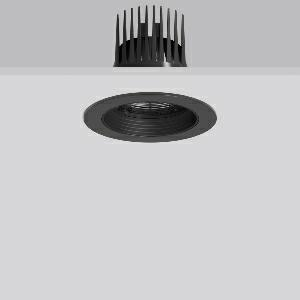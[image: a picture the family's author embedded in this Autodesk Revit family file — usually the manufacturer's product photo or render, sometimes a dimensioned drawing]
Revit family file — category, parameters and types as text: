
# Revit family: heledon_maxi_e_901781_003_3351
name_source: partatom
category: Lighting Fixtures
units: mm (PartAtom-declared; Revit-internal decimal feet)

## family parameters
Cut with Voids When Loaded = No
Host = Face
Light Source = No
Part Type = Normal
Room Calculation Point = No
Round Connector Dimension = Use Diameter
Shared = No

## types (1)
- HELEDON maxi E (1 x LED Modul 920 meat+, 1900 lm, 2000)
    Apparent Load = 33 VA
    Approval mark = CE
    CIE Flux Codes = 97 100 100 100 100
    Color Rendering = 90
    Color Temperature = 2000
    Default Elevation = 1800 mm
    Description = Series: HELEDON maxi
Round recessed downlight. Housing: die-cast aluminium, powder-coated. Black plastic ring and recessed LED to prevent glare from the side. Optical assembly with lens made of plastic (polycarbonate) for the best homogeneous light distribution - can be changed without tools. Special LED for illumination of meat included. Suitable for Recessed ceiling mounting. Installation without tools thanks to spring fastening system. Including separate LED converter with connecting cable 600 mm.High quality converter without flickering and stroboscopic effect. Through-wiring box (5 pole) available as accessory. The following accessories can be mounted without use of tools: interchangeable lenses, decorative glasses, honeycomb louvre, clear and frosted diffusers, white interchangeable plastic ring. 
Colour: deep black, matt (RAL 9005)
Diameter: 162 mm
Height: 3 mm
Cut-out diameter: 152 mm
Recess height: 200 mm
Luminaire: recess height: 135 mm
Lamp: LED
Socket: without socket
Colour temperature: meat +
System power: 33 W
Rated luminous flux: 1900 lm
Luminous efficiency: 58 lm/W
Control gear: Regulated power supply
Protection class: II
Type of protection: IP 20
    Height = 0 mm  [stored 0 ft]
    Lamp = 1 x LED Modul 920 meat+
    Lamp Light Flux = 1900 lm
    Lamp count = 1
    Length = 162 mm
    Lifetime = 50000 h
    Luminous efficacy = 58 lm/W
    Manufacturer = RZB
    ModVariant = No
    Model = 901781.003
    Mounting Place = Ceiling
    Mounting Type = Recessed
    Number of Poles = 1
    OnlyDefault = Yes
    Power Factor = 1
    Product Name = HELEDON maxi E
    Product group = Recessed downlights
    ProductGroupID = 402
    Protection Class = Protection class II
    Protection Degree = IP 20
    RLX_Detail_Level = 1
    RLX_Emergency_Light_Flux = 0 lm
    RLX_Emergency_Type = 0
    RLX_Emergency_Type_DB = No
    RlxData = <blob elided: 122113 chars, md5=103aec59>
    Socket = socket
    Standby Power = 0 W
    System Light Flux = 1900 lm
    System Power = 33 W
    Type Comments = Product without accessories
    Type Image = 901663.003.jpg
    URL = http://relux.com
    VarID = ---
    Voltage = 230 V
    Voltage Range = 220-240 V
    Weight = 0.00 kg
    Width = 0 mm  [stored 0 ft]

note: [stored X ft] marks values corroborated as IEEE doubles in the binary element streams (Revit-internal decimal feet)

## geometry (parser evidence)
native form markers: Blend x4, Sweep x11
no freeform markers — native parametric forms only
